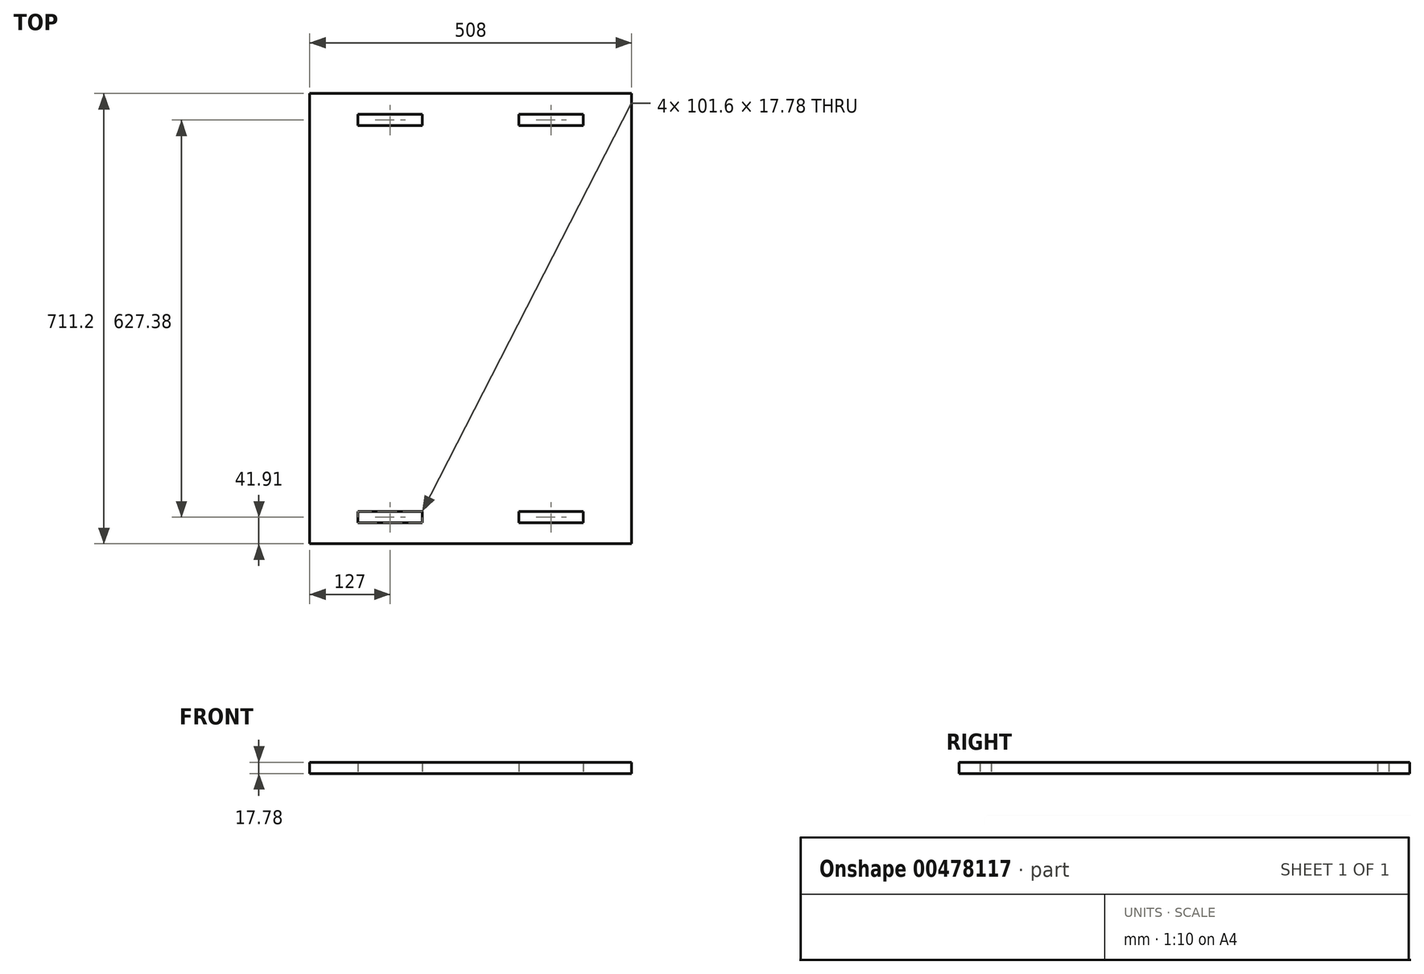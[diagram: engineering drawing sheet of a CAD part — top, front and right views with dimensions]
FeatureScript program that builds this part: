
annotation { "Feature Type Name" : "Feature", "Feature Type Description" : "" }
export const myFeature = defineFeature(function(context is Context, id is Id, definition is map)
    precondition{}
    {
        {
            var Q0;
            Q0=qCreatedBy(makeId("Top.planeOp"),FACE);
            var sketch = newSketch(context, id + "F0", { "sketchPlane" : qUnion([Q0])});
            skLineSegment(sketch, "E0.bottom", {"start": v(0, 0) * mm, "end": v(508, 0) * mm});
            skLineSegment(sketch, "E0.top", {"start": v(0, 711.2) * mm, "end": v(508, 711.2) * mm});
            skLineSegment(sketch, "E0.left", {"start": v(0, 0) * mm, "end": v(0, 711.2) * mm});
            skLineSegment(sketch, "E0.right", {"start": v(508, 0) * mm, "end": v(508, 711.2) * mm});
            skLineSegment(sketch, "E1", {"start": v(0, 711.2) * mm, "end": v(0, 660.4) * mm});
            skLineSegment(sketch, "E2", {"start": v(0, 711.2) * mm, "end": v(254, 711.2) * mm});
            skPoint(sketch, "E3", {"position": v(127, 660.4) * mm});
            skLineSegment(sketch, "E4", {"start": v(127, 660.4) * mm, "end": v(177.8, 660.4) * mm});
            skLineSegment(sketch, "E5", {"start": v(127, 660.4) * mm, "end": v(76.2, 660.4) * mm});
            skLineSegment(sketch, "E6", {"start": v(76.2, 660.4) * mm, "end": v(76.2, 678.18) * mm});
            skLineSegment(sketch, "E7", {"start": v(76.2, 678.18) * mm, "end": v(177.8, 678.18) * mm});
            skLineSegment(sketch, "E8", {"start": v(177.8, 678.18) * mm, "end": v(177.8, 660.4) * mm});
            skPoint(sketch, "E9", {"position": v(381, 660.4) * mm});
            skLineSegment(sketch, "E10", {"start": v(381, 660.4) * mm, "end": v(431.8, 660.4) * mm});
            skLineSegment(sketch, "E11", {"start": v(381, 660.4) * mm, "end": v(330.2, 660.4) * mm});
            skLineSegment(sketch, "E12", {"start": v(330.2, 660.4) * mm, "end": v(330.2, 678.18) * mm});
            skLineSegment(sketch, "E13", {"start": v(330.2, 678.18) * mm, "end": v(431.8, 678.18) * mm});
            skLineSegment(sketch, "E14", {"start": v(431.8, 678.18) * mm, "end": v(431.8, 660.4) * mm});
            skLineSegment(sketch, "E15", {"start": v(0, 711.2) * mm, "end": v(0, 355.6) * mm});
            skLineSegment(sketch, "E16", {"start": v(0, 355.6) * mm, "end": v(508, 355.6) * mm});
            skLineSegment(sketch, "E17.MirrorCS", {"start": v(330.2, 50.8) * mm, "end": v(330.2, 33.02) * mm});
            skLineSegment(sketch, "E18.MirrorCS", {"start": v(177.8, 33.02) * mm, "end": v(177.8, 50.8) * mm});
            skLineSegment(sketch, "E19.MirrorCS", {"start": v(431.8, 33.02) * mm, "end": v(431.8, 50.8) * mm});
            skLineSegment(sketch, "E20.MirrorCS", {"start": v(76.2, 50.8) * mm, "end": v(76.2, 33.02) * mm});
            skLineSegment(sketch, "E21.MirrorCS", {"start": v(381, 50.8) * mm, "end": v(330.2, 50.8) * mm});
            skLineSegment(sketch, "E22.MirrorCS", {"start": v(381, 50.8) * mm, "end": v(431.8, 50.8) * mm});
            skPoint(sketch, "E23.MirrorP", {"position": v(381, 50.8) * mm});
            skLineSegment(sketch, "E24.MirrorCS", {"start": v(330.2, 33.02) * mm, "end": v(431.8, 33.02) * mm});
            skLineSegment(sketch, "E25.MirrorCS", {"start": v(127, 50.8) * mm, "end": v(76.2, 50.8) * mm});
            skLineSegment(sketch, "E26.MirrorCS", {"start": v(76.2, 33.02) * mm, "end": v(177.8, 33.02) * mm});
            skPoint(sketch, "E27.MirrorP", {"position": v(127, 50.8) * mm});
            skLineSegment(sketch, "E28.MirrorCS", {"start": v(127, 50.8) * mm, "end": v(177.8, 50.8) * mm});
            skSolve(sketch);
        }
        {
            var Q0;
            {var subQ0=sQuery(id+"F0.wireOp",EDGE,"E0.bottom");Q0=makeQuery(id+"F0.imprint","IMPRINT",FACE,{"disambiguationData":[TD([[makeQuery(id+"F0.imprint","IMPRINT",EDGE,{"derivedFrom":subQ0}),1.0]])]});}
            var Q1;
            {var subQ0=sQuery(id+"F0.wireOp",EDGE,"E0.top");Q1=makeQuery(id+"F0.imprint","IMPRINT",FACE,{"disambiguationData":[TD([[makeQuery(id+"F0.imprint","IMPRINT",EDGE,{"derivedFrom":subQ0}),-1.0]])]});}
            extrude(context, id + "F1", {"entities" : qUnion([Q0, Q1]), "depth" : 17.78 * mm});
        }
    });
